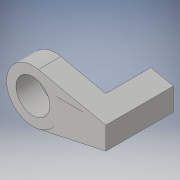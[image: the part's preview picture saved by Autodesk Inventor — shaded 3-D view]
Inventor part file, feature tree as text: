
AUTODESK INVENTOR PART (.ipt)
format: ipt  version: 2016 (Build 200138000, 138)  size: 296,960 bytes
history: native  units: in
note: dims shown in document units (in); Inventor stores cm internally (conversion verified against a paired STEP export)
features: extrude x5, sketch x5
ambient origin geometry x8: Origin, YZ Plane, XZ Plane, XY Plane, X Axis, Y Axis, Z Axis, Center Point
bodies: Solid1 (feature_tree)
feature tree (10):
  extrude  "Extrusion1"  Depth=0.2756in
  extrude  "Extrusion2"  Depth=0.1181in TaperAngle=0.0deg
  extrude  "Extrusion5"  Depth=0.2362in TaperAngle=0.0deg
  extrude  "Extrusion7"  Depth=0.1181in TaperAngle=0.0deg
  extrude  "Extrusion8"  Depth=0.2362in TaperAngle=0.0deg
  sketch  "Sketch1"  dims[d0=0.1772in d1=0.2756in]
  sketch  "Sketch2"  dims[d3=0.2756in d5=0.1181in d6=0.0in]
  sketch  "Sketch6"  dims[d7=0.1181in d8=0.2362in d9=0.0in]
  sketch  "Sketch8"  dims[d13=0.1181in d16=0.1181in d17=0.0in]
  sketch  "Sketch9"  dims[d27=0.1181in d28=0.0in d29=0.2362in d30=0.0in]
